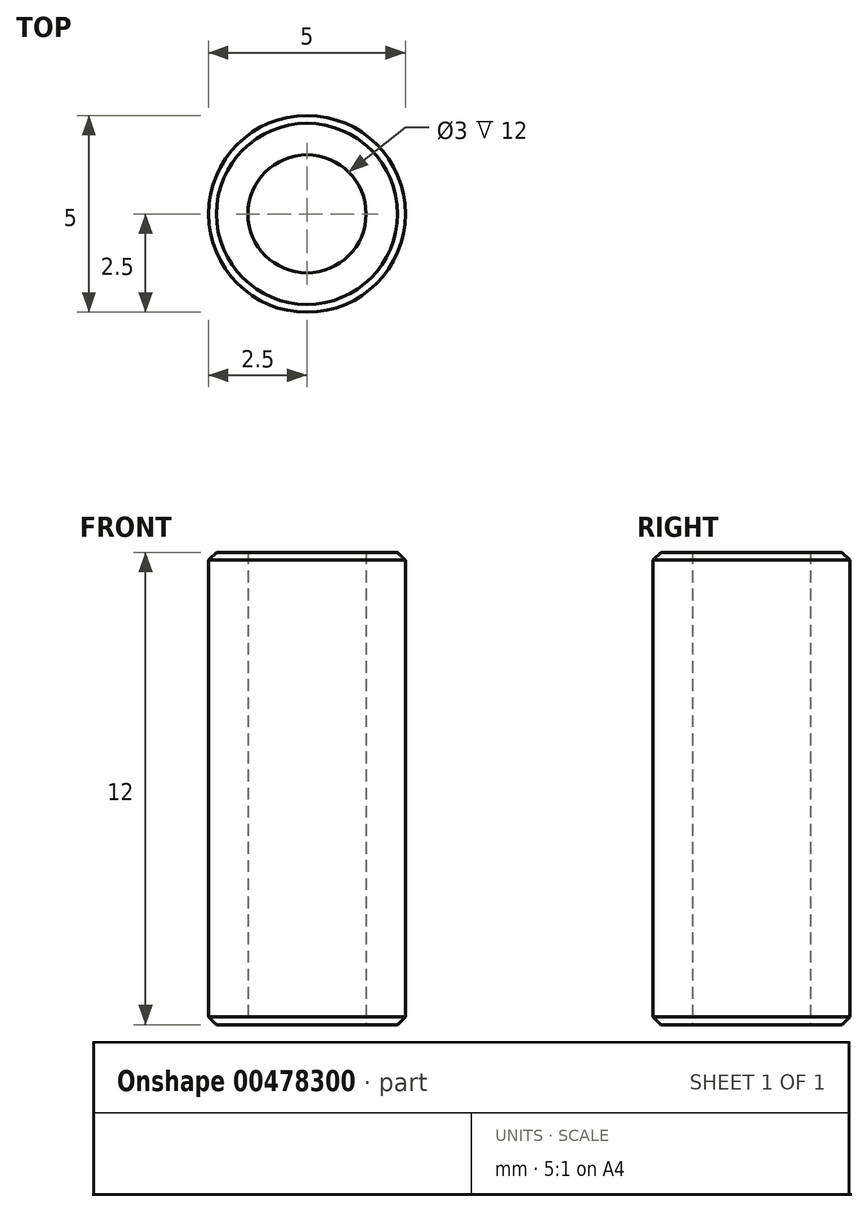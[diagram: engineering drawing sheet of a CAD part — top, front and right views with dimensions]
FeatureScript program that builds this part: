
annotation { "Feature Type Name" : "Feature", "Feature Type Description" : "" }
export const myFeature = defineFeature(function(context is Context, id is Id, definition is map)
    precondition{}
    {
        {
            var Q0;
            Q0=qCreatedBy(makeId("Top.planeOp"),FACE);
            var sketch = newSketch(context, id + "F0", { "sketchPlane" : qUnion([Q0])});
            skCircle(sketch, "E0", {"center": v(0, 0) * mm, "radius": 2.5 * mm});
            skSolve(sketch);
        }
        {
            var Q0;
            Q0 = qSketchRegion(id + "F0", true);
            extrude(context, id + "F1", {"entities" : qUnion([Q0]), "depth" : 12 * mm});
        }
        {
            var Q0;
            Q0=makeQuery(id+"F1.opExtrude","CAP_FACE",FACE,{"disambiguationData":[OSD([sQuery(id+"F0.wireOp",EDGE,"E0")])],"isStart":false});
            var Q1;
            Q1=makeQuery(id+"F1.opExtrude","CAP_FACE",FACE,{"disambiguationData":[OSD([sQuery(id+"F0.wireOp",EDGE,"E0")])],"isStart":true});
            chamfer(context, id + "F2", {"entities" : qUnion([Q0, Q1]), "width" : 0.2 * mm, "tangentPropagation" : true});
        }
        {
            var Q0;
            Q0=sQuery(id+"F0.wireOp",VERTEX,"E0.center");
            var Q1;
            Q1=makeQuery(id+"F1.opExtrude","SWEPT_BODY",BODY,{"disambiguationData":[OSD([sQuery(id+"F0.wireOp",EDGE,"E0")])]});
            hole(context, id + "F3", {"style" : HoleStyle.SIMPLE, "endStyle" : HoleEndStyle.THROUGH, "oppositeDirection" : true, "holeDiameter" : 3 * mm, "isTappedThrough" : true, "tappedDepth" : 12 * mm, "tapClearance" : 3, "startFromSketch" : true, "locations" : qUnion([Q0]), "scope" : qUnion([Q1])});
        }
    });
